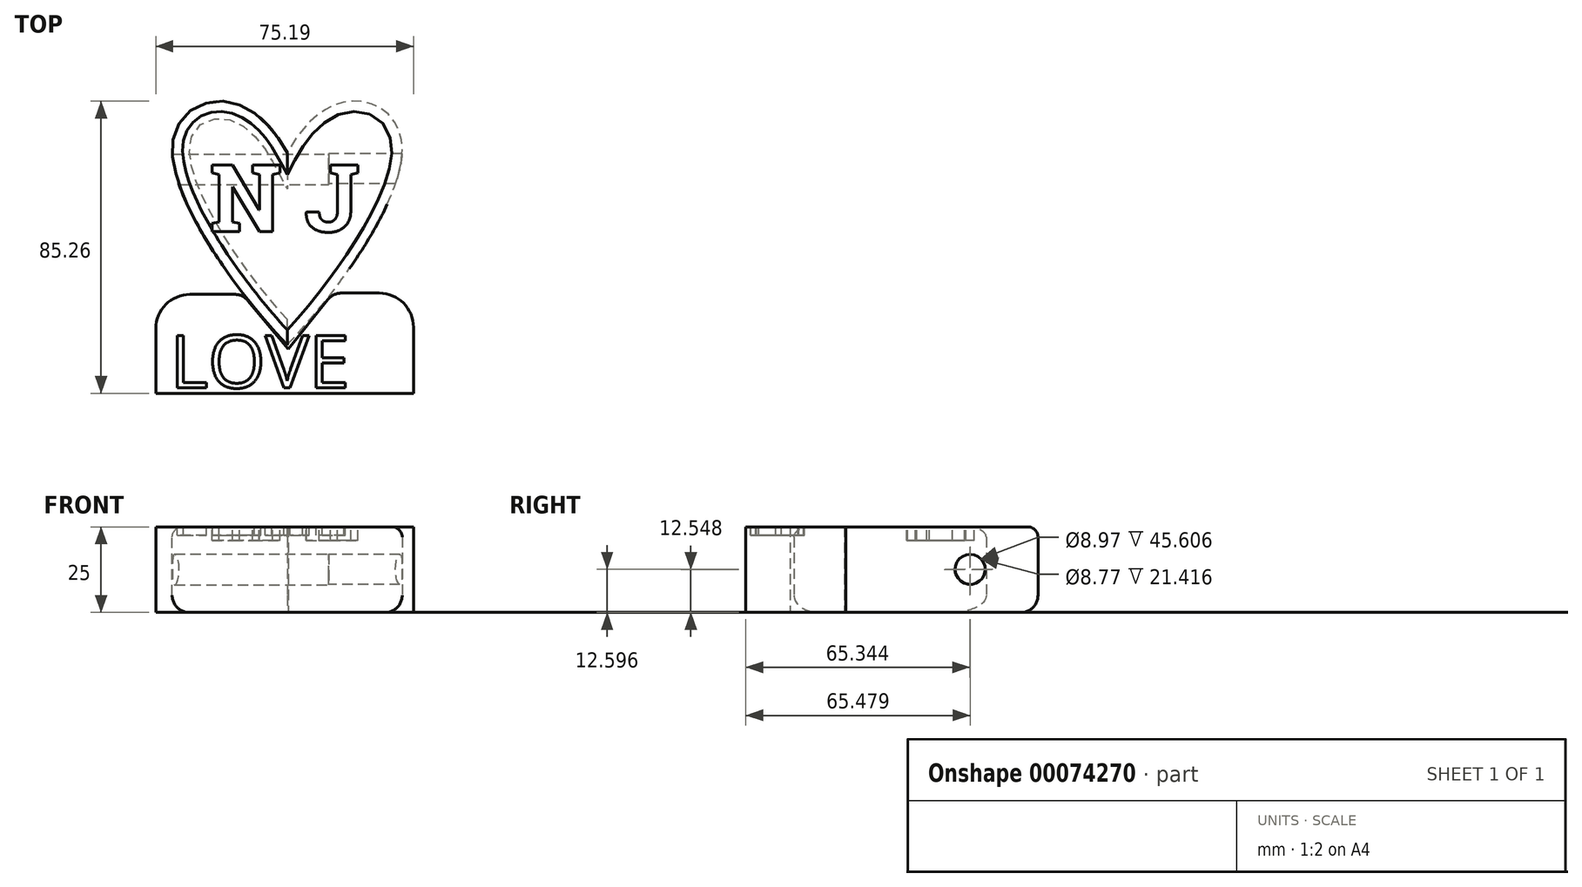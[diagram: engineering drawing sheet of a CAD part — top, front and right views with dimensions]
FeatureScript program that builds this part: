
annotation { "Feature Type Name" : "Feature", "Feature Type Description" : "" }
export const myFeature = defineFeature(function(context is Context, id is Id, definition is map)
    precondition{}
    {
        {
            var Q0;
            Q0=qCreatedBy(makeId("Top.planeOp"),FACE);
            var sketch = newSketch(context, id + "F0", { "sketchPlane" : qUnion([Q0])});
            skFitSpline(sketch, "E0", {"points": [v(-12.1, -40.61) * mm, v(-45.65, 16.38) * mm, v(-35.5, 30.07) * mm, v(-12.1, 15.46) * mm], "startDerivative": vector(-103.7, 108.8) * mm, "endDerivative": vector(71.26, -131.24) * mm});
            skLineSegment(sketch, "E1", {"start": v(-12.1, -40.61) * mm, "end": v(-12.1, 15.46) * mm});
            skSolve(sketch);
        }
        {
            var Q0;
            Q0=makeQuery(id+"F0.imprint","IMPRINT",FACE,{"disambiguationData":[TD([[makeQuery(id+"F0.imprint","IMPRINT",EDGE,{"derivedFrom":sQuery(id+"F0.wireOp",EDGE,"E0")}),-1.0]])]});
            extrude(context, id + "F1", {"entities" : qUnion([Q0]), "depth" : 25 * mm});
        }
        {
            var Q0;
            Q0=makeQuery(id+"F1.opExtrude","SWEPT_BODY",BODY,{"disambiguationData":[OSD([sQuery(id+"F0.wireOp",EDGE,"E0"),sQuery(id+"F0.wireOp",EDGE,"E1")])]});
            var Q1;
            Q1=makeQuery(id+"F1.opExtrude","SWEPT_FACE",FACE,{"disambiguationData":[OSD([sQuery(id+"F0.wireOp",EDGE,"E1")])]});
            mirror(context, id + "F2", {"operationType" : NewBodyOperationType.ADD, "entities" : qUnion([Q0]), "mirrorPlane" : qUnion([Q1])});
        }
        {
            var Q0;
            Q0=qCreatedBy(makeId("Top.planeOp"),FACE);
            var sketch = newSketch(context, id + "F3", { "sketchPlane" : qUnion([Q0])});
            skLineSegment(sketch, "E2", {"start": v(-50.43, -25.87) * mm, "end": v(-25.04, -25.87) * mm});
            skLineSegment(sketch, "E3", {"start": v(-25.04, -25.87) * mm, "end": v(-11.78, -41.83) * mm});
            skLineSegment(sketch, "E4", {"start": v(-11.78, -41.83) * mm, "end": v(1.3, -25.48) * mm});
            skLineSegment(sketch, "E5", {"start": v(1.3, -25.48) * mm, "end": v(24.76, -25.48) * mm});
            skLineSegment(sketch, "E6", {"start": v(24.76, -25.48) * mm, "end": v(24.76, -54.71) * mm});
            skLineSegment(sketch, "E7", {"start": v(24.76, -54.71) * mm, "end": v(-50.43, -54.71) * mm});
            skLineSegment(sketch, "E8", {"start": v(-50.43, -54.71) * mm, "end": v(-50.43, -25.87) * mm});
            skSolve(sketch);
        }
        {
            var Q0;
            Q0=makeQuery(id+"F3.imprint","IMPRINT",FACE,{"disambiguationData":[TD([[makeQuery(id+"F3.imprint","IMPRINT",EDGE,{"derivedFrom":sQuery(id+"F3.wireOp",EDGE,"E2")}),-1.0]])]});
            extrude(context, id + "F4", {"entities" : qUnion([Q0]), "depth" : 25 * mm});
        }
        {
            var Q0;
            Q0=qCreatedBy(makeId("Right.planeOp"),FACE);
            var sketch = newSketch(context, id + "F5", { "sketchPlane" : qUnion([Q0])});
            skCircle(sketch, "E9", {"center": v(10.63, 12.55) * mm, "radius": 4.49 * mm});
            skSolve(sketch);
        }
        {
            var Q0;
            Q0 = qSketchRegion(id + "F5", true);
            extrude(context, id + "F6", {"entities" : qUnion([Q0]), "operationType" : NewBodyOperationType.REMOVE, "oppositeDirection" : true, "depth" : 63.08 * mm});
        }
        {
            var Q0;
            Q0=qCreatedBy(makeId("Right.planeOp"),FACE);
            var sketch = newSketch(context, id + "F7", { "sketchPlane" : qUnion([Q0])});
            skCircle(sketch, "E10", {"center": v(10.77, 12.6) * mm, "radius": 4.39 * mm});
            skSolve(sketch);
        }
        {
            var Q0;
            Q0 = qSketchRegion(id + "F7", true);
            extrude(context, id + "F8", {"entities" : qUnion([Q0]), "operationType" : NewBodyOperationType.REMOVE, "depth" : 25 * mm});
        }
        {
            var Q0;
            Q0=makeQuery(id+"F1.opExtrude","CAP_EDGE",EDGE,{"disambiguationData":[OSD([sQuery(id+"F0.wireOp",EDGE,"E0")])],"isStart":false});
            var Q1;
            Q1=makeQuery(id+"F2.opPattern","COPY",EDGE,{"derivedFrom":makeQuery(id+"F1.opExtrude","CAP_EDGE",EDGE,{"disambiguationData":[OSD([sQuery(id+"F0.wireOp",EDGE,"E0")])],"isStart":false}),"instanceName":"1"});
            fillet(context, id + "F9", {"entities" : qUnion([Q0, Q1]), "radius" : 3 * mm, "tangentPropagation" : true, "allowEdgeOverflow" : false});
        }
        {
            var Q0;
            Q0=makeQuery(id+"F1.opExtrude","CAP_EDGE",EDGE,{"disambiguationData":[OSD([sQuery(id+"F0.wireOp",EDGE,"E0")])],"isStart":true});
            var Q1;
            Q1=makeQuery(id+"F2.opPattern","COPY",EDGE,{"derivedFrom":makeQuery(id+"F1.opExtrude","CAP_EDGE",EDGE,{"disambiguationData":[OSD([sQuery(id+"F0.wireOp",EDGE,"E0")])],"isStart":true}),"instanceName":"1"});
            fillet(context, id + "F16", {"entities" : qUnion([Q0, Q1]), "radius" : 5 * mm, "tangentPropagation" : true, "allowEdgeOverflow" : false});
        }
        {
            var Q0;
            Q0=makeQuery(id+"F4.opExtrude","CAP_FACE",FACE,{"disambiguationData":[OSD([sQuery(id+"F3.wireOp",EDGE,"E2"),sQuery(id+"F3.wireOp",EDGE,"E3"),sQuery(id+"F3.wireOp",EDGE,"E4"),sQuery(id+"F3.wireOp",EDGE,"E5"),sQuery(id+"F3.wireOp",EDGE,"E6"),sQuery(id+"F3.wireOp",EDGE,"E7"),sQuery(id+"F3.wireOp",EDGE,"E8")])],"isStart":false});
            var sketch = newSketch(context, id + "F10", { "sketchPlane" : qUnion([Q0])});
            skText(sketch, "E11", { "text": "LOVE", "fontName": "OpenSans-Regular.ttf"});
            const initialGuessF10  = {"E11": [-0.04629, -0.05316, 1, 0, 0.01543]};
            skSetInitialGuess(sketch, initialGuessF10);
            skSolve(sketch);
        }
        {
            var Q0;
            Q0=makeQuery(id+"F10.imprint","IMPRINT",FACE,{"disambiguationData":[TD([[makeQuery(id+"F10.imprint","IMPRINT",EDGE,{"derivedFrom":sQuery(id+"F10.wireOp",EDGE,"E11.sketch_text.stroke-0")}),-1.0]])]});
            var Q1;
            Q1=makeQuery(id+"F10.imprint","IMPRINT",FACE,{"disambiguationData":[TD([[makeQuery(id+"F10.imprint","IMPRINT",EDGE,{"derivedFrom":sQuery(id+"F10.wireOp",EDGE,"E11.sketch_text.stroke-6")}),-1.0]])]});
            var Q2;
            Q2=makeQuery(id+"F10.imprint","IMPRINT",FACE,{"disambiguationData":[TD([[makeQuery(id+"F10.imprint","IMPRINT",EDGE,{"derivedFrom":sQuery(id+"F10.wireOp",EDGE,"E11.sketch_text.stroke-22")}),-1.0]])]});
            var Q3;
            Q3=makeQuery(id+"F10.imprint","IMPRINT",FACE,{"disambiguationData":[TD([[makeQuery(id+"F10.imprint","IMPRINT",EDGE,{"derivedFrom":sQuery(id+"F10.wireOp",EDGE,"E11.sketch_text.stroke-31")}),-1.0]])]});
            extrude(context, id + "F11", {"entities" : qUnion([Q0, Q1, Q2, Q3]), "operationType" : NewBodyOperationType.REMOVE, "oppositeDirection" : true, "depth" : 2.5 * mm});
        }
        {
            var Q0;
            {var subQ0=makeQuery(id+"F1.opExtrude","CAP_FACE",FACE,{"disambiguationData":[OSD([sQuery(id+"F0.wireOp",EDGE,"E0"),sQuery(id+"F0.wireOp",EDGE,"E1")])],"isStart":false});Q0=makeQuery(id+"F2.boolean.opBoolean","MERGE",FACE,{"derivedFrom":[subQ0,makeQuery(id+"F2.opPattern","COPY",FACE,{"derivedFrom":subQ0,"instanceName":"1"})]});}
            var sketch = newSketch(context, id + "F12", { "sketchPlane" : qUnion([Q0])});
            skText(sketch, "E12", { "text": "N J", "fontName": "RobotoSlab-Bold.ttf"});
            const initialGuessF12  = {"E12": [-0.0348, -0.0075, 1, 0, 0.01966]};
            skSetInitialGuess(sketch, initialGuessF12);
            skSolve(sketch);
        }
        {
            var Q0;
            Q0=makeQuery(id+"F12.imprint","IMPRINT",FACE,{"disambiguationData":[TD([[makeQuery(id+"F12.imprint","IMPRINT",EDGE,{"derivedFrom":sQuery(id+"F12.wireOp",EDGE,"E12.sketch_text.stroke-24")}),-1.0]])]});
            var Q1;
            {var subQ0=sQuery(id+"F12.wireOp",EDGE,"E12.sketch_text.stroke-10");var subQ1=sQuery(id+"F12.wireOp",EDGE,"E12.sketch_text.stroke-9");var subQ2=makeQuery(id+"F12.imprint","INTERSECT",VERTEX,{"derivedFrom":[subQ1,subQ0]});Q1=makeQuery(id+"F12.imprint","IMPRINT",FACE,{"disambiguationData":[TD([[makeQuery(id+"F12.imprint","IMPRINT",EDGE,{"disambiguationData":[TD([[subQ2,1.0]])],"derivedFrom":subQ1}),-1.0]])]});}
            var Q2;
            Q2=makeQuery(id+"F12.imprint","IMPRINT",FACE,{"disambiguationData":[TD([[makeQuery(id+"F12.imprint","IMPRINT",EDGE,{"derivedFrom":sQuery(id+"F12.wireOp",EDGE,"E12.sketch_text.stroke-0")}),-1.0]])]});
            extrude(context, id + "F13", {"entities" : qUnion([Q0, Q1, Q2]), "operationType" : NewBodyOperationType.REMOVE, "oppositeDirection" : true, "depth" : 4 * mm});
        }
        {
            var Q0;
            Q0=makeQuery(id+"F4.opExtrude","SWEPT_EDGE",EDGE,{"disambiguationData":[OSD([sQuery(id+"F3.wireOp",EDGE,"E2"),sQuery(id+"F3.wireOp",EDGE,"E8")])]});
            var Q1;
            Q1=makeQuery(id+"F4.opExtrude","SWEPT_EDGE",EDGE,{"disambiguationData":[OSD([sQuery(id+"F3.wireOp",EDGE,"E5"),sQuery(id+"F3.wireOp",EDGE,"E6")])]});
            fillet(context, id + "F14", {"entities" : qUnion([Q0, Q1]), "radius" : 10 * mm, "tangentPropagation" : true, "allowEdgeOverflow" : false});
        }
        {
            var Q0;
            Q0=makeQuery(id+"F4.opExtrude","SWEPT_EDGE",EDGE,{"disambiguationData":[OSD([sQuery(id+"F3.wireOp",EDGE,"E2"),sQuery(id+"F3.wireOp",EDGE,"E3")])]});
            var Q1;
            Q1=makeQuery(id+"F4.opExtrude","SWEPT_EDGE",EDGE,{"disambiguationData":[OSD([sQuery(id+"F3.wireOp",EDGE,"E4"),sQuery(id+"F3.wireOp",EDGE,"E5")])]});
            fillet(context, id + "F15", {"entities" : qUnion([Q0, Q1]), "radius" : 5 * mm, "tangentPropagation" : true, "allowEdgeOverflow" : false});
        }
    });
